# Revit family: WHBF4-WF1-EG10
name_source: partatom
category: Mechanical Equipment
revit_build: Autodesk Revit MEP 2016 (Build: 20150220_1215(x64)
units: mm (PartAtom-declared; Revit-internal decimal feet)

## family parameters
Cut with Voids When Loaded = No
Host = Face
OmniClass Number = 23.65.70.11.11
OmniClass Title = Fixtures for Liquids
Part Type = Normal
Room Calculation Point = No
Round Connector Dimension = Use Diameter
Shared = Yes

## types (1)
- WHBF4-WF1-EG10
    Amperage = 0
    CW Connection = Yes
    Default Elevation = 36 "
    Description = Sensor Activated Ligature Resistant Cup Filler
    HW Connection = No
    MGRD-E501 = Yes
    Manufacturer = WHITEHALL
    Material = Stainless Steel
    Model = WHBF4-WF1-EG10
    OVERALL DEPTH = 28
    OVERALL SIZE HEIGHT = 6
    OVERALL SIZE WIDTH = 18.25
    Revised Date = 04/10/18
    Tempered Water Connection = No
    URL = https://www.acorneng.com
    Vent Connection = No
    Voltage = 0
    Waste Connection = Yes

## geometry (parser evidence)
native form markers: Sweep x3
no freeform markers — native parametric forms only
